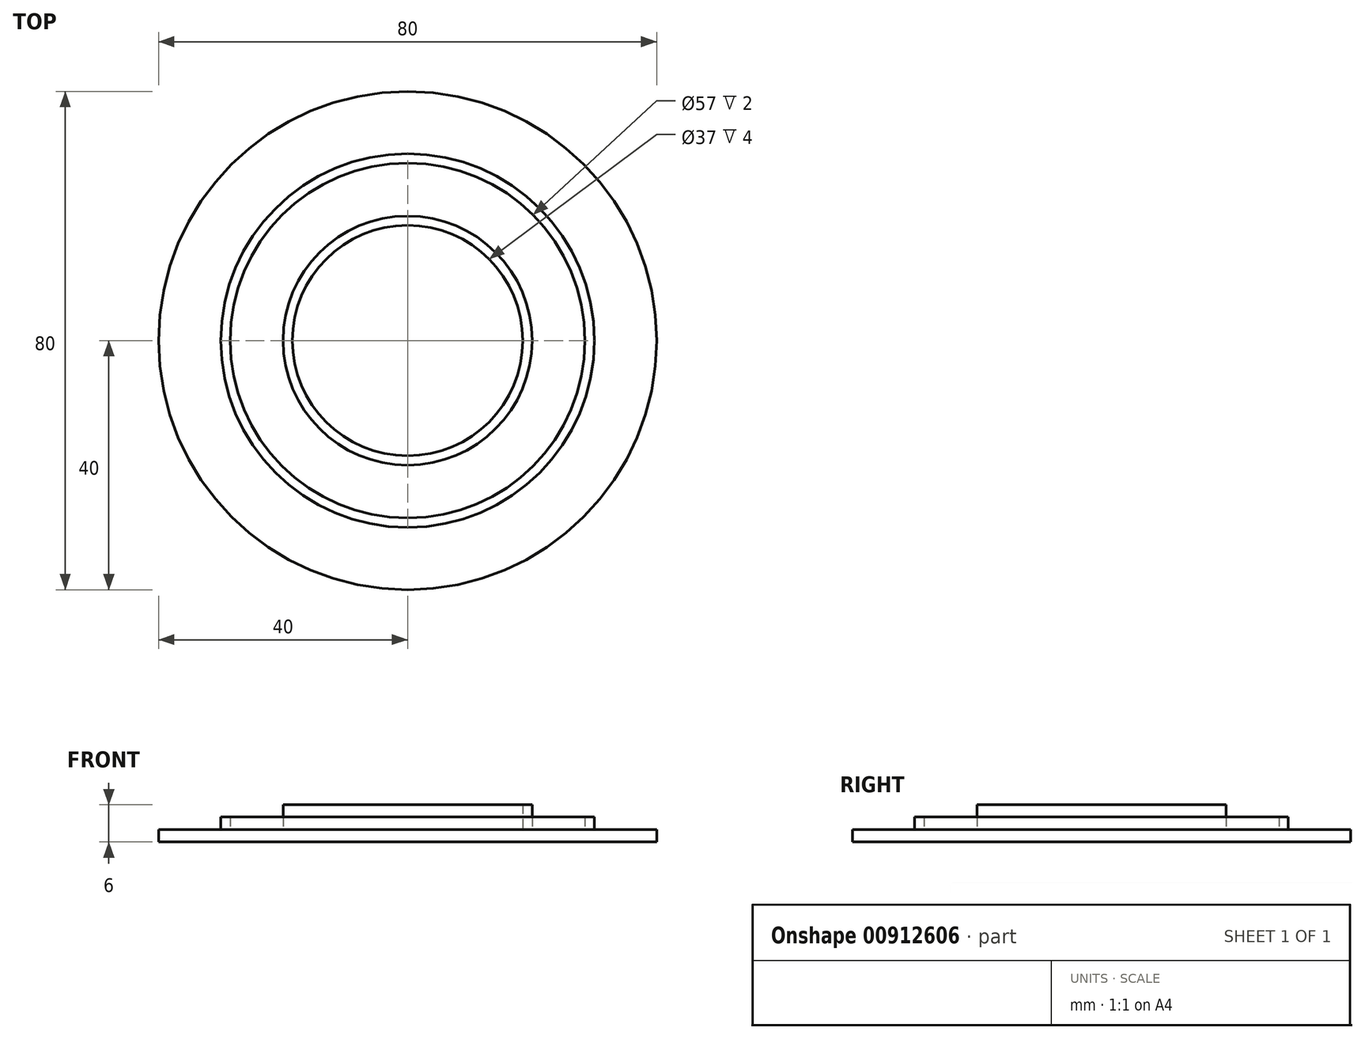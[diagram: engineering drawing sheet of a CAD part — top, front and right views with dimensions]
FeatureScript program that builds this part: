
annotation { "Feature Type Name" : "Feature", "Feature Type Description" : "" }
export const myFeature = defineFeature(function(context is Context, id is Id, definition is map)
    precondition{}
    {
        {
            var Q0;
            Q0=qCreatedBy(makeId("Top.planeOp"),FACE);
            var sketch = newSketch(context, id + "F0", { "sketchPlane" : qUnion([Q0])});
            skCircle(sketch, "E0", {"center": v(0, 0) * mm, "radius": 40 * mm});
            skSolve(sketch);
        }
        {
            var Q0;
            Q0 = qSketchRegion(id + "F0", true);
            extrude(context, id + "F1", {"entities" : qUnion([Q0]), "depth" : 2 * mm, "offsetDistance" : 25 * mm});
        }
        {
            var Q0;
            Q0=makeQuery(id+"F1.opExtrude","CAP_FACE",FACE,{"disambiguationData":[OSD([sQuery(id+"F0.wireOp",EDGE,"E0")])],"isStart":false});
            var sketch = newSketch(context, id + "F2", { "sketchPlane" : qUnion([Q0])});
            skCircle(sketch, "E1", {"center": v(0, 0) * mm, "radius": 30 * mm});
            skCircle(sketch, "E2", {"center": v(0, 0) * mm, "radius": 28.5 * mm});
            skSolve(sketch);
        }
        {
            var Q0;
            Q0 = qSketchRegion(id + "F2", true);
            extrude(context, id + "F3", {"entities" : qUnion([Q0]), "operationType" : NewBodyOperationType.ADD, "depth" : 2 * mm, "offsetDistance" : 25 * mm});
        }
        {
            var Q0;
            Q0=makeQuery(id+"F3.boolean.opBoolean","SPLIT",FACE,{"disambiguationData":[TD([makeQuery(id+"F3.opExtrude","SWEPT_FACE",FACE,{"disambiguationData":[OSD([sQuery(id+"F2.wireOp",EDGE,"E2")])]})])],"derivedFrom":makeQuery(id+"F1.opExtrude","CAP_FACE",FACE,{"disambiguationData":[OSD([sQuery(id+"F0.wireOp",EDGE,"E0")])],"isStart":false})});
            var sketch = newSketch(context, id + "F4", { "sketchPlane" : qUnion([Q0])});
            skCircle(sketch, "E3", {"center": v(0, 0) * mm, "radius": 20 * mm});
            skCircle(sketch, "E4", {"center": v(0, 0) * mm, "radius": 18.5 * mm});
            skSolve(sketch);
        }
        {
            var Q0;
            Q0 = qSketchRegion(id + "F4", true);
            extrude(context, id + "F5", {"entities" : qUnion([Q0]), "operationType" : NewBodyOperationType.ADD, "depth" : 4 * mm, "offsetDistance" : 25 * mm});
        }
    });
